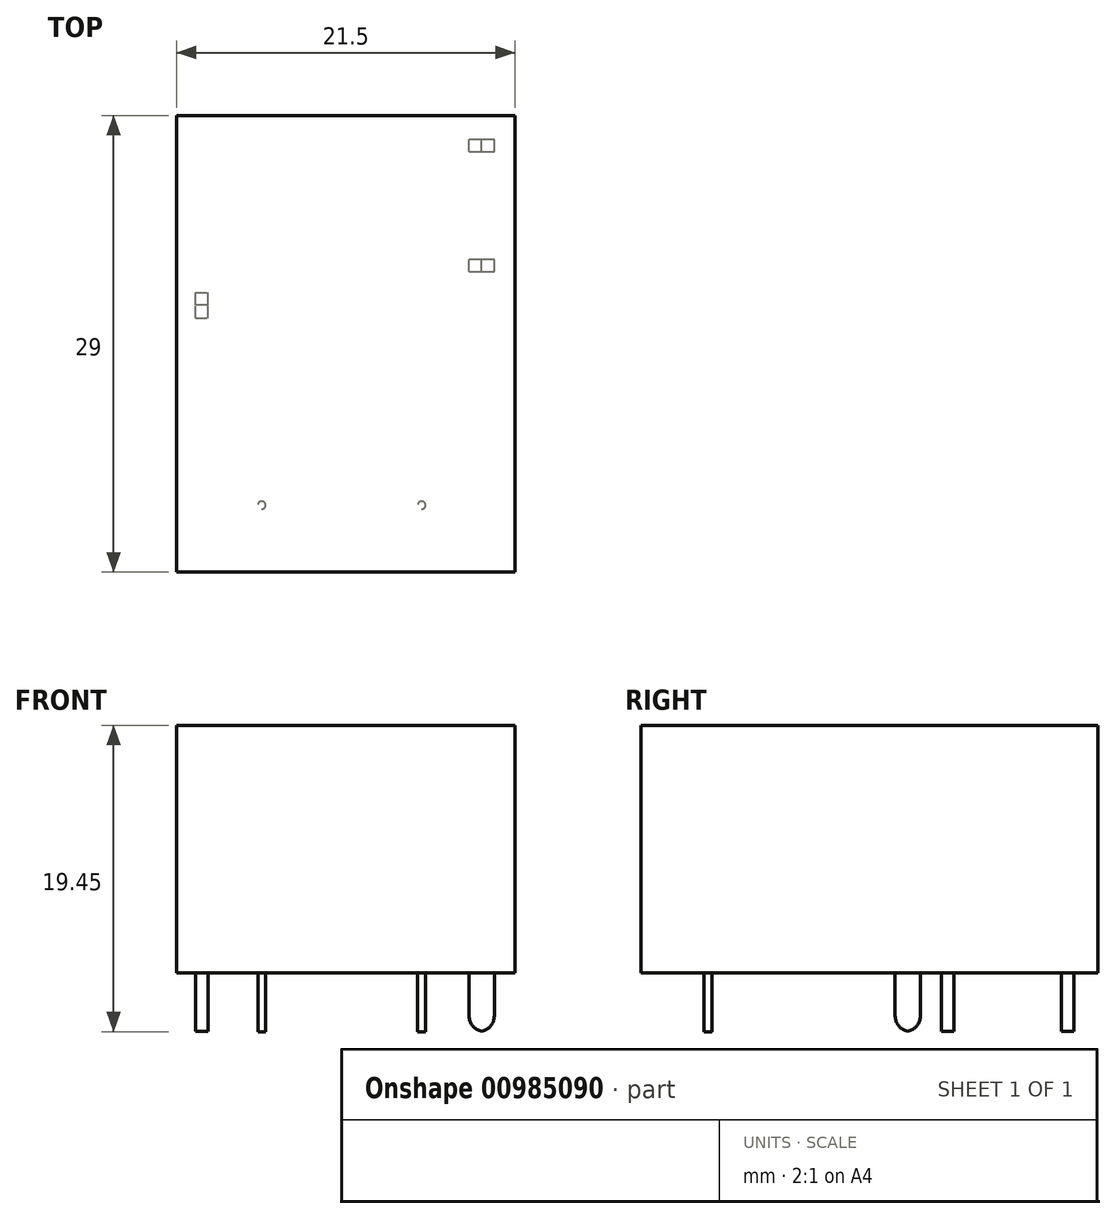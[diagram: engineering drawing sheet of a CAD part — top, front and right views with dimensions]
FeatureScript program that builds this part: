
annotation { "Feature Type Name" : "Feature", "Feature Type Description" : "" }
export const myFeature = defineFeature(function(context is Context, id is Id, definition is map)
    precondition{}
    {
        {
            var Q0;
            Q0=qCreatedBy(makeId("Top.planeOp"),FACE);
            var sketch = newSketch(context, id + "F0", { "sketchPlane" : qUnion([Q0])});
            skLineSegment(sketch, "E0.bottom", {"start": v(10.75, 14.5) * mm, "end": v(-10.75, 14.5) * mm});
            skLineSegment(sketch, "E0.top", {"start": v(10.75, -14.5) * mm, "end": v(-10.75, -14.5) * mm});
            skLineSegment(sketch, "E0.left", {"start": v(10.75, 14.5) * mm, "end": v(10.75, -14.5) * mm});
            skLineSegment(sketch, "E0.right", {"start": v(-10.75, 14.5) * mm, "end": v(-10.75, -14.5) * mm});
            skSolve(sketch);
        }
        {
            var Q0;
            Q0=makeQuery(id+"F0.imprint","IMPRINT",FACE,{"disambiguationData":[TD([[makeQuery(id+"F0.imprint","IMPRINT",EDGE,{"derivedFrom":sQuery(id+"F0.wireOp",EDGE,"E0.bottom")}),1.0]])]});
            extrude(context, id + "F1", {"entities" : qUnion([Q0]), "depth" : 15.7 * mm, "offsetDistance" : 25 * mm});
        }
        {
            var Q0;
            Q0=makeQuery(id+"F0.imprint","IMPRINT",FACE,{"disambiguationData":[TD([[makeQuery(id+"F0.imprint","IMPRINT",EDGE,{"derivedFrom":sQuery(id+"F0.wireOp",EDGE,"E0.bottom")}),1.0]])]});
            var sketch = newSketch(context, id + "F2", { "sketchPlane" : qUnion([Q0])});
            skLineSegment(sketch, "E1.bottom", {"start": v(7.83, 12.2) * mm, "end": v(9.43, 12.2) * mm});
            skLineSegment(sketch, "E1.top", {"start": v(7.83, 13) * mm, "end": v(9.43, 13) * mm});
            skLineSegment(sketch, "E1.left", {"start": v(7.83, 12.2) * mm, "end": v(7.83, 13) * mm});
            skLineSegment(sketch, "E1.right", {"start": v(9.43, 12.2) * mm, "end": v(9.43, 13) * mm});
            skPoint(sketch, "E1.middle", {"position": v(8.63, 12.6) * mm});
            skLineSegment(sketch, "E2.bottom", {"start": v(7.83, 4.58) * mm, "end": v(9.43, 4.58) * mm});
            skLineSegment(sketch, "E2.top", {"start": v(7.83, 5.38) * mm, "end": v(9.43, 5.38) * mm});
            skLineSegment(sketch, "E2.left", {"start": v(7.83, 4.58) * mm, "end": v(7.83, 5.38) * mm});
            skLineSegment(sketch, "E2.right", {"start": v(9.43, 4.58) * mm, "end": v(9.43, 5.38) * mm});
            skPoint(sketch, "E2.middle", {"position": v(8.63, 4.98) * mm});
            skCircle(sketch, "E3", {"center": v(-5.34, -10.26) * mm, "radius": 0.25 * mm});
            skCircle(sketch, "E4", {"center": v(4.82, -10.26) * mm, "radius": 0.25 * mm});
            skLineSegment(sketch, "E5.bottom", {"start": v(-9.55, 1.64) * mm, "end": v(-8.75, 1.64) * mm});
            skLineSegment(sketch, "E5.top", {"start": v(-9.55, 3.24) * mm, "end": v(-8.75, 3.24) * mm});
            skLineSegment(sketch, "E5.left", {"start": v(-9.55, 1.64) * mm, "end": v(-9.55, 3.24) * mm});
            skLineSegment(sketch, "E5.right", {"start": v(-8.75, 1.64) * mm, "end": v(-8.75, 3.24) * mm});
            skPoint(sketch, "E5.middle", {"position": v(-9.15, 2.44) * mm});
            skSolve(sketch);
        }
        {
            var Q0;
            Q0 = qSketchRegion(id + "F2", true);
            extrude(context, id + "F3", {"entities" : qUnion([Q0]), "oppositeDirection" : true, "depth" : 3.75 * mm, "offsetDistance" : 25 * mm});
        }
        {
            var Q0;
            Q0=makeQuery(id+"F3.opExtrude","CAP_EDGE",EDGE,{"disambiguationData":[OSD([sQuery(id+"F2.wireOp",EDGE,"E1.left")])],"isStart":false});
            var Q1;
            Q1=makeQuery(id+"F3.opExtrude","CAP_EDGE",EDGE,{"disambiguationData":[OSD([sQuery(id+"F2.wireOp",EDGE,"E1.right")])],"isStart":false});
            var Q2;
            Q2=makeQuery(id+"F3.opExtrude","CAP_EDGE",EDGE,{"disambiguationData":[OSD([sQuery(id+"F2.wireOp",EDGE,"E2.left")])],"isStart":false});
            var Q3;
            Q3=makeQuery(id+"F3.opExtrude","CAP_EDGE",EDGE,{"disambiguationData":[OSD([sQuery(id+"F2.wireOp",EDGE,"E2.right")])],"isStart":false});
            var Q4;
            Q4=makeQuery(id+"F3.opExtrude","CAP_EDGE",EDGE,{"disambiguationData":[OSD([sQuery(id+"F2.wireOp",EDGE,"E5.bottom")])],"isStart":false});
            var Q5;
            Q5=makeQuery(id+"F3.opExtrude","CAP_EDGE",EDGE,{"disambiguationData":[OSD([sQuery(id+"F2.wireOp",EDGE,"E5.top")])],"isStart":false});
            fillet(context, id + "F4", {"entities" : qUnion([Q0, Q1, Q2, Q3, Q4, Q5]), "radius" : 1 * mm, "tangentPropagation" : true, "allowEdgeOverflow" : false});
        }
    });
